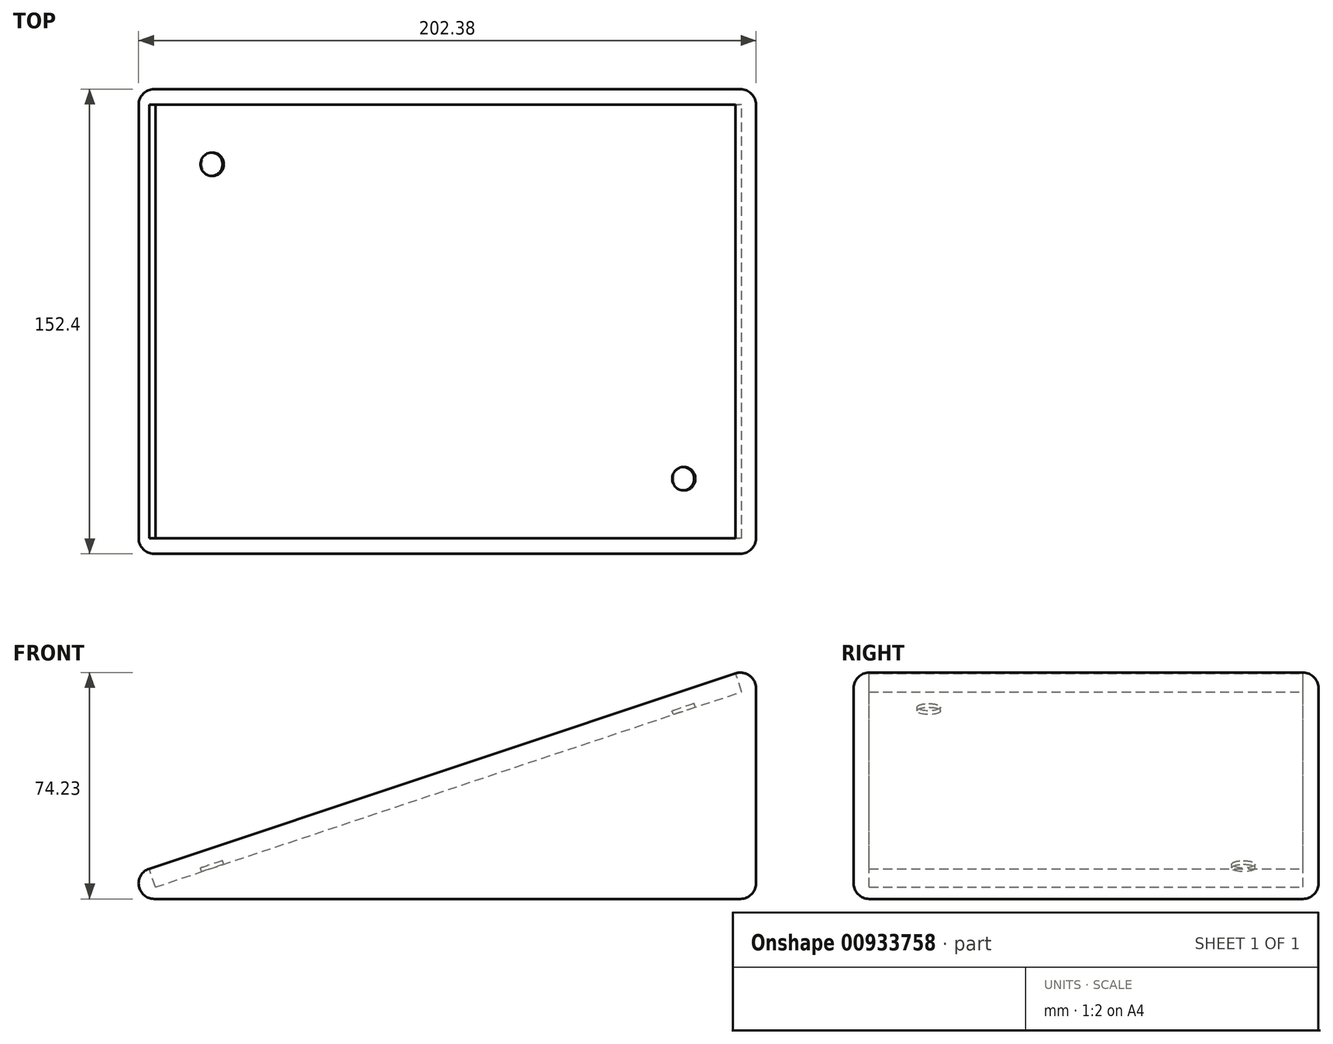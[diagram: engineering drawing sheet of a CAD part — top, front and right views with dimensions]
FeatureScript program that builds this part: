
annotation { "Feature Type Name" : "Feature", "Feature Type Description" : "" }
export const myFeature = defineFeature(function(context is Context, id is Id, definition is map)
    precondition{}
    {
        {
            var Q0;
            Q0=qCreatedBy(makeId("Top.planeOp"),FACE);
            var sketch = newSketch(context, id + "F0", { "sketchPlane" : qUnion([Q0])});
            skLineSegment(sketch, "E0.bottom", {"start": v(114.3, -76.2) * mm, "end": v(-114.3, -76.2) * mm});
            skLineSegment(sketch, "E0.top", {"start": v(114.3, 76.2) * mm, "end": v(-114.3, 76.2) * mm});
            skLineSegment(sketch, "E0.left", {"start": v(114.3, -76.2) * mm, "end": v(114.3, 76.2) * mm});
            skLineSegment(sketch, "E0.right", {"start": v(-114.3, -76.2) * mm, "end": v(-114.3, 76.2) * mm});
            skPoint(sketch, "E0.middle", {"position": v(0, 0) * mm});
            skSolve(sketch);
        }
        {
            var Q0;
            Q0=makeQuery(id+"F0.imprint","IMPRINT",FACE,{"disambiguationData":[TD([[makeQuery(id+"F0.imprint","IMPRINT",EDGE,{"derivedFrom":sQuery(id+"F0.wireOp",EDGE,"E0.bottom")}),-1.0]])]});
            extrude(context, id + "F1", {"entities" : qUnion([Q0]), "depth" : 76.2 * mm, "offsetDistance" : 25.4 * mm});
        }
        {
            var Q0;
            Q0=makeQuery(id+"F1.opExtrude","SWEPT_FACE",FACE,{"disambiguationData":[OSD([sQuery(id+"F0.wireOp",EDGE,"E0.bottom")])]});
            var sketch = newSketch(context, id + "F2", { "sketchPlane" : qUnion([Q0])});
            skLineSegment(sketch, "E1", {"start": v(-114.3, 0) * mm, "end": v(114.3, 76.2) * mm});
            skSolve(sketch);
        }
        {
            var Q0;
            Q0=makeQuery(id+"F2.imprint","IMPRINT",FACE,{"disambiguationData":[TD([[makeQuery(id+"F2.imprint","IMPRINT",EDGE,{"derivedFrom":sQuery(id+"F2.wireOp",EDGE,"E1")}),1.0]])]});
            extrude(context, id + "F3", {"entities" : qUnion([Q0]), "operationType" : NewBodyOperationType.REMOVE, "oppositeDirection" : true, "depth" : 152.4 * mm, "offsetDistance" : 25.4 * mm});
        }
        {
            var Q0;
            Q0=makeQuery(id+"F3.boolean.opBoolean","COPY",FACE,{"derivedFrom":makeQuery(id+"F3.opExtrude","SWEPT_FACE",FACE,{"disambiguationData":[OSD([sQuery(id+"F2.wireOp",EDGE,"E1")])]})});
            var Q1;
            Q1=makeQuery(id+"F1.opExtrude","SWEPT_FACE",FACE,{"disambiguationData":[OSD([sQuery(id+"F0.wireOp",EDGE,"E0.left")])]});
            var Q2;
            Q2=makeQuery(id+"F1.opExtrude","SWEPT_FACE",FACE,{"disambiguationData":[OSD([sQuery(id+"F0.wireOp",EDGE,"E0.top")])]});
            var Q3;
            Q3=makeQuery(id+"F1.opExtrude","SWEPT_FACE",FACE,{"disambiguationData":[OSD([sQuery(id+"F0.wireOp",EDGE,"E0.bottom")])]});
            fillet(context, id + "F4", {"entities" : qUnion([Q0, Q1, Q2, Q3]), "radius" : 5.08 * mm, "tangentPropagation" : true, "allowEdgeOverflow" : false});
        }
        {
            var Q0;
            Q0=makeQuery(id+"F3.boolean.opBoolean","COPY",FACE,{"derivedFrom":makeQuery(id+"F3.opExtrude","SWEPT_FACE",FACE,{"disambiguationData":[OSD([sQuery(id+"F2.wireOp",EDGE,"E1")])]})});
            var sketch = newSketch(context, id + "F5", { "sketchPlane" : qUnion([Q0])});
            skCircle(sketch, "E2", {"center": v(105.66, 51.58) * mm, "radius": 3.81 * mm});
            skLineSegment(sketch, "E3", {"start": v(125.48, 0) * mm, "end": v(-77.13, 0) * mm, "construction": true});
            skLineSegment(sketch, "E4", {"start": v(24.18, 71.12) * mm, "end": v(24.18, -71.12) * mm, "construction": true});
            skCircle(sketch, "E5.MirrorC", {"center": v(105.66, -51.58) * mm, "radius": 3.81 * mm});
            skCircle(sketch, "E6.MirrorC", {"center": v(-57.3, 51.58) * mm, "radius": 3.81 * mm});
            skCircle(sketch, "E7.MirrorC", {"center": v(-57.3, -51.58) * mm, "radius": 3.81 * mm});
            skCircle(sketch, "E8", {"center": v(24.18, 0) * mm, "radius": 3.81 * mm});
            skSolve(sketch);
        }
        {
            var Q0;
            Q0=makeQuery(id+"F5.imprint","IMPRINT",FACE,{"disambiguationData":[TD([[makeQuery(id+"F5.imprint","IMPRINT",EDGE,{"derivedFrom":sQuery(id+"F5.wireOp",EDGE,"E5.MirrorC")}),-1.0]])]});
            var Q1;
            Q1=makeQuery(id+"F5.imprint","IMPRINT",FACE,{"disambiguationData":[TD([[makeQuery(id+"F5.imprint","IMPRINT",EDGE,{"derivedFrom":sQuery(id+"F5.wireOp",EDGE,"E2")}),1.0]])]});
            var Q2;
            Q2=makeQuery(id+"F5.imprint","IMPRINT",FACE,{"disambiguationData":[TD([[makeQuery(id+"F5.imprint","IMPRINT",EDGE,{"derivedFrom":sQuery(id+"F5.wireOp",EDGE,"E8")}),1.0]])]});
            var Q3;
            Q3=makeQuery(id+"F5.imprint","IMPRINT",FACE,{"disambiguationData":[TD([[makeQuery(id+"F5.imprint","IMPRINT",EDGE,{"derivedFrom":sQuery(id+"F5.wireOp",EDGE,"E6.MirrorC")}),-1.0]])]});
            var Q4;
            Q4=makeQuery(id+"F5.imprint","IMPRINT",FACE,{"disambiguationData":[TD([[makeQuery(id+"F5.imprint","IMPRINT",EDGE,{"derivedFrom":sQuery(id+"F5.wireOp",EDGE,"E7.MirrorC")}),1.0]])]});
            extrude(context, id + "F6", {"entities" : qUnion([Q0, Q1, Q2, Q3, Q4]), "operationType" : NewBodyOperationType.REMOVE, "oppositeDirection" : true, "depth" : 6.35 * mm, "offsetDistance" : 25.4 * mm});
        }
        {
            var Q0;
            Q0=makeQuery(id+"F3.boolean.opBoolean","COPY",FACE,{"derivedFrom":makeQuery(id+"F3.opExtrude","SWEPT_FACE",FACE,{"disambiguationData":[OSD([sQuery(id+"F2.wireOp",EDGE,"E1")])]})});
            extrude(context, id + "F7", {"entities" : qUnion([Q0]), "operationType" : NewBodyOperationType.REMOVE, "oppositeDirection" : true, "depth" : 5.08 * mm, "offsetDistance" : 25.4 * mm});
        }
    });
